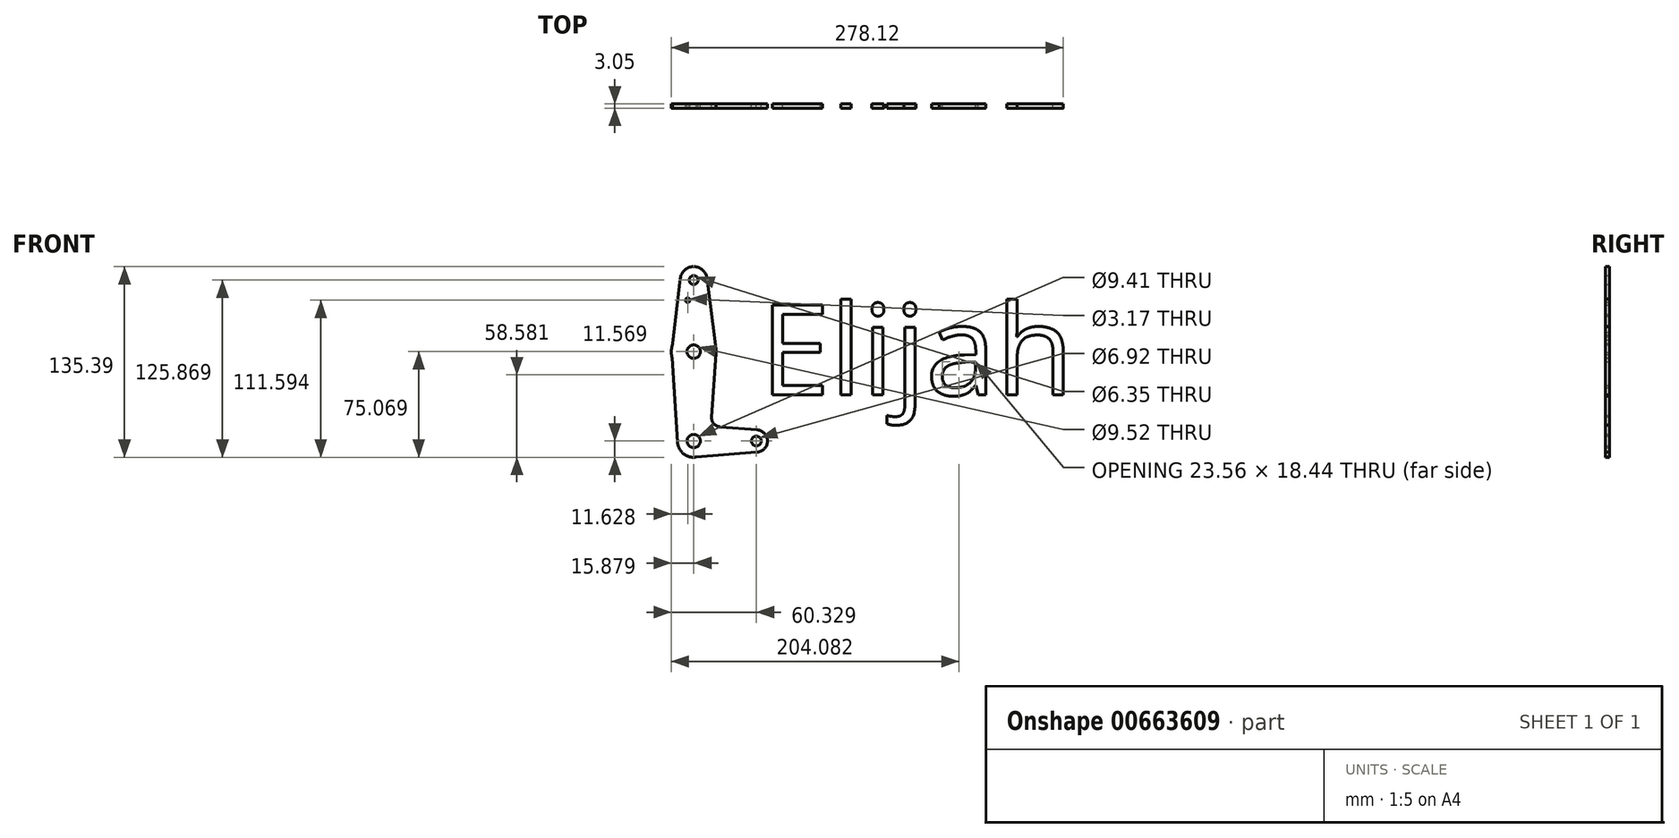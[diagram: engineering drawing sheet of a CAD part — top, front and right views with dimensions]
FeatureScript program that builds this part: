
annotation { "Feature Type Name" : "Feature", "Feature Type Description" : "" }
export const myFeature = defineFeature(function(context is Context, id is Id, definition is map)
    precondition{}
    {
        {
            var Q0;
            Q0=qCreatedBy(makeId("Front.planeOp"),FACE);
            var sketch = newSketch(context, id + "F0", { "sketchPlane" : qUnion([Q0])});
            skLineSegment(sketch, "E0", {"start": v(-52.87, -52.77) * mm, "end": v(-8.42, -52.77) * mm, "construction": true});
            skCircle(sketch, "E1", {"center": v(-52.87, 61.53) * mm, "radius": 9.53 * mm});
            skCircle(sketch, "E2", {"center": v(-8.42, -52.77) * mm, "radius": 7.94 * mm});
            skCircle(sketch, "E3", {"center": v(-52.87, -52.77) * mm, "radius": 11.56 * mm});
            skCircle(sketch, "E4", {"center": v(-52.87, 10.73) * mm, "radius": 15.88 * mm});
            skLineSegment(sketch, "E5", {"start": v(-43.42, 62.72) * mm, "end": v(-37.12, 12.71) * mm});
            skLineSegment(sketch, "E6", {"start": v(-62.33, 62.62) * mm, "end": v(-67.67, 16.46) * mm});
            skLineSegment(sketch, "E7", {"start": v(-37.03, 9.65) * mm, "end": v(-40.14, -35.95) * mm});
            skLineSegment(sketch, "E8", {"start": v(-68.14, 6.4) * mm, "end": v(-64.41, -53.5) * mm});
            skLineSegment(sketch, "E9", {"start": v(-34.31, -42.71) * mm, "end": v(-7.78, -44.86) * mm});
            skLineSegment(sketch, "E10", {"start": v(-52.87, -64.34) * mm, "end": v(-8.42, -60.7) * mm});
            skCircle(sketch, "E11", {"center": v(-52.87, 61.53) * mm, "radius": 3.18 * mm});
            skCircle(sketch, "E12", {"center": v(-52.87, 10.73) * mm, "radius": 4.76 * mm});
            skCircle(sketch, "E13", {"center": v(-52.87, -52.77) * mm, "radius": 4.7 * mm});
            skCircle(sketch, "E14", {"center": v(-8.42, -52.77) * mm, "radius": 3.46 * mm});
            skArc(sketch, "E15.filletArc", {"start": v(-40.14, -35.95) * mm, "mid": v(-38.61, -40.53) * mm, "end": v(-34.31, -42.71) * mm});
            skLineSegment(sketch, "E16", {"start": v(-52.87, -52.77) * mm, "end": v(-52.87, 61.53) * mm, "construction": true});
            skCircle(sketch, "E17", {"center": v(-57.12, 47.25) * mm, "radius": 1.59 * mm});
            skText(sketch, "E18", { "text": "Elijah", "fontName": "OpenSans-Regular.ttf"});
            const initialGuessF0  = {"E18": [-0.00592, -0.0201, 1, 0, 0.06447]};
            skSetInitialGuess(sketch, initialGuessF0);
            skSolve(sketch);
        }
        {
            var Q0;
            Q0 = qSketchRegion(id + "F0", true);
            extrude(context, id + "F1", {"entities" : qUnion([Q0]), "depth" : 3.05 * mm, "offsetDistance" : 25.4 * mm});
        }
    });
